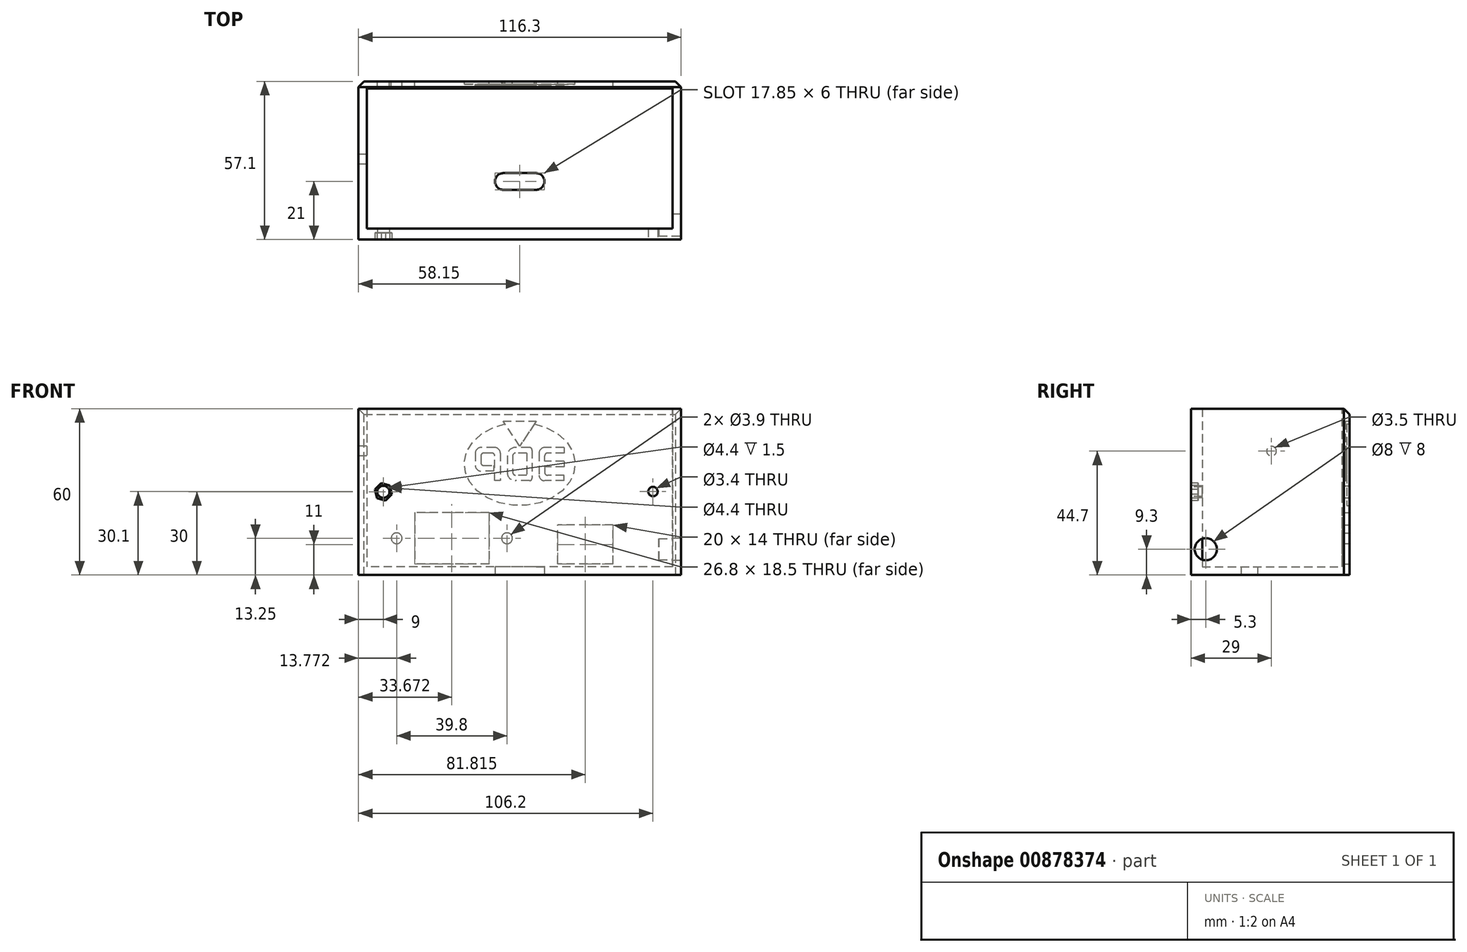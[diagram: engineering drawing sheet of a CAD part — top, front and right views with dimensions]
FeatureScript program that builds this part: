
annotation { "Feature Type Name" : "Feature", "Feature Type Description" : "" }
export const myFeature = defineFeature(function(context is Context, id is Id, definition is map)
    precondition{}
    {
        {
            var Q0;
            Q0=qCreatedBy(makeId("Front.planeOp"),FACE);
            var sketch = newSketch(context, id + "F0", { "sketchPlane" : qUnion([Q0])});
            skLineSegment(sketch, "E0.bottom", {"start": v(0, 0) * mm, "end": v(116.3, 0) * mm});
            skLineSegment(sketch, "E0.top", {"start": v(0, 70) * mm, "end": v(116.3, 70) * mm});
            skLineSegment(sketch, "E0.left", {"start": v(0, 0) * mm, "end": v(0, 70) * mm});
            skLineSegment(sketch, "E0.right", {"start": v(116.3, 0) * mm, "end": v(116.3, 70) * mm});
            skCircle(sketch, "E1", {"center": v(18, 61.5) * mm, "radius": 1.7 * mm});
            skCircle(sketch, "E2", {"center": v(103.3, 61.5) * mm, "radius": 1.7 * mm});
            skCircle(sketch, "E3", {"center": v(106.2, 5.1) * mm, "radius": 1.7 * mm});
            skCircle(sketch, "E4", {"center": v(9, 5) * mm, "radius": 2.2 * mm});
            skLineSegment(sketch, "E5.top", {"start": v(116.3, 0) * mm, "end": v(119.3, 0) * mm});
            skPoint(sketch, "E6.orphan", {"position": v(-3, 70) * mm});
            skPoint(sketch, "E7.right.end.orphan", {"position": v(-3, 35) * mm});
            skPoint(sketch, "E8.right.end.orphan", {"position": v(119.3, 35) * mm});
            skPoint(sketch, "E5.bottom.end.orphan", {"position": v(119.3, 70) * mm});
            skPoint(sketch, "E9.top.end.orphan", {"position": v(-3, 0) * mm});
            skSolve(sketch);
        }
        {
            var Q0;
            Q0=makeQuery(id+"F0.imprint","IMPRINT",FACE,{"disambiguationData":[TD([[makeQuery(id+"F0.imprint","IMPRINT",EDGE,{"derivedFrom":sQuery(id+"F0.wireOp",EDGE,"E0.bottom")}),1.0]])]});
            extrude(context, id + "F1", {"entities" : qUnion([Q0]), "oppositeDirection" : true, "depth" : 4 * mm});
        }
        {
            var Q0;
            Q0=makeQuery(id+"F1.opExtrude","CAP_FACE",FACE,{"disambiguationData":[OSD([sQuery(id+"F0.wireOp",EDGE,"E0.bottom"),sQuery(id+"F0.wireOp",EDGE,"E0.top"),sQuery(id+"F0.wireOp",EDGE,"E0.left"),sQuery(id+"F0.wireOp",EDGE,"E0.right"),sQuery(id+"F0.wireOp",EDGE,"E1"),sQuery(id+"F0.wireOp",EDGE,"E2"),sQuery(id+"F0.wireOp",EDGE,"E3"),sQuery(id+"F0.wireOp",EDGE,"E4")])],"isStart":false});
            var sketch = newSketch(context, id + "F2", { "sketchPlane" : qUnion([Q0])});
            skPoint(sketch, "E10.oppositeSnap0", {"position": v(-116.3, 35) * mm});
            skLineSegment(sketch, "E10.top", {"start": v(-116.3, 35) * mm, "end": v(-113.3, 35) * mm});
            skLineSegment(sketch, "E10.left", {"start": v(-116.3, 0) * mm, "end": v(-116.3, 35) * mm});
            skLineSegment(sketch, "E10.right", {"start": v(-113.3, 0) * mm, "end": v(-113.3, 35) * mm});
            skPoint(sketch, "E11.oppositeSnap0", {"position": v(0, 35) * mm});
            skLineSegment(sketch, "E11.top", {"start": v(0, 35) * mm, "end": v(-3, 35) * mm});
            skLineSegment(sketch, "E11.left", {"start": v(0, 0) * mm, "end": v(0, 35) * mm});
            skLineSegment(sketch, "E11.right", {"start": v(-3, 0) * mm, "end": v(-3, 35) * mm});
            skLineSegment(sketch, "E12.top", {"start": v(-116.3, -25) * mm, "end": v(-113.3, -25) * mm});
            skLineSegment(sketch, "E12.left", {"start": v(-116.3, 0) * mm, "end": v(-116.3, -25) * mm});
            skLineSegment(sketch, "E12.right", {"start": v(-113.3, 0) * mm, "end": v(-113.3, -25) * mm});
            skLineSegment(sketch, "E13.top", {"start": v(0, -25) * mm, "end": v(-3, -25) * mm});
            skLineSegment(sketch, "E13.left", {"start": v(0, 0) * mm, "end": v(0, -25) * mm});
            skLineSegment(sketch, "E13.right", {"start": v(-3, 0) * mm, "end": v(-3, -25) * mm});
            skSolve(sketch);
        }
        {
            var Q0;
            Q0=qSketchRegion(id+"F2",true);
            extrude(context, id + "F3", {"entities" : qUnion([Q0]), "operationType" : NewBodyOperationType.ADD, "depth" : 53.1 * mm});
        }
        {
            var Q0;
            Q0=makeQuery(id+"F3.boolean.opBoolean","MERGE",FACE,{"derivedFrom":[makeQuery(id+"F1.opExtrude","SWEPT_FACE",FACE,{"disambiguationData":[OSD([sQuery(id+"F0.wireOp",EDGE,"E0.left")])]}),makeQuery(id+"F3.opExtrude","SWEPT_FACE",FACE,{"disambiguationData":[OSD([sQuery(id+"F2.wireOp",EDGE,"E11.left"),sQuery(id+"F2.wireOp",EDGE,"E13.left")])]})]});
            var sketch = newSketch(context, id + "F4", { "sketchPlane" : qUnion([Q0])});
            skLineSegment(sketch, "E14", {"start": v(-57.1, 35) * mm, "end": v(-57.1, -25) * mm});
            skLineSegment(sketch, "E15", {"start": v(-57.1, -25) * mm, "end": v(0, -25) * mm});
            skLineSegment(sketch, "E16", {"start": v(0, -25) * mm, "end": v(0, 0) * mm});
            skLineSegment(sketch, "E17", {"start": v(0, 0) * mm, "end": v(-4, 0) * mm});
            skLineSegment(sketch, "E18", {"start": v(-4, 0) * mm, "end": v(-4, -22) * mm});
            skLineSegment(sketch, "E19", {"start": v(-4, -22) * mm, "end": v(-54.5, -22) * mm});
            skLineSegment(sketch, "E20", {"start": v(-54.5, -22) * mm, "end": v(-54.5, 35) * mm});
            skLineSegment(sketch, "E21", {"start": v(-54.5, 35) * mm, "end": v(-57.1, 35) * mm});
            skSolve(sketch);
        }
        {
            var Q0;
            Q0=qSketchRegion(id+"F4",true);
            extrude(context, id + "F5", {"entities" : qUnion([Q0]), "operationType" : NewBodyOperationType.ADD, "oppositeDirection" : true, "depth" : 116.3 * mm});
        }
        {
            var Q0;
            Q0=makeQuery(id+"F5.boolean.opBoolean","MERGE",FACE,{"derivedFrom":[makeQuery(id+"F3.opExtrude","CAP_FACE",FACE,{"disambiguationData":[OSD([sQuery(id+"F2.wireOp",EDGE,"E10.top"),sQuery(id+"F2.wireOp",EDGE,"E10.left"),sQuery(id+"F2.wireOp",EDGE,"E10.right"),sQuery(id+"F2.wireOp",EDGE,"E12.top"),sQuery(id+"F2.wireOp",EDGE,"E12.left"),sQuery(id+"F2.wireOp",EDGE,"E12.right")])],"isStart":false}),makeQuery(id+"F3.opExtrude","CAP_FACE",FACE,{"disambiguationData":[OSD([sQuery(id+"F2.wireOp",EDGE,"E11.top"),sQuery(id+"F2.wireOp",EDGE,"E11.left"),sQuery(id+"F2.wireOp",EDGE,"E11.right"),sQuery(id+"F2.wireOp",EDGE,"E13.top"),sQuery(id+"F2.wireOp",EDGE,"E13.left"),sQuery(id+"F2.wireOp",EDGE,"E13.right")])],"isStart":false}),makeQuery(id+"F5.opExtrude","SWEPT_FACE",FACE,{"disambiguationData":[OSD([sQuery(id+"F4.wireOp",EDGE,"E14")])]})]});
            var sketch = newSketch(context, id + "F6", { "sketchPlane" : qUnion([Q0])});
            skLineSegment(sketch, "E22.bottom", {"start": v(-47.07, -2.5) * mm, "end": v(-20.27, -2.5) * mm});
            skLineSegment(sketch, "E22.top", {"start": v(-47.07, -21) * mm, "end": v(-20.27, -21) * mm});
            skLineSegment(sketch, "E22.left", {"start": v(-47.07, -2.5) * mm, "end": v(-47.07, -21) * mm});
            skLineSegment(sketch, "E22.right", {"start": v(-20.27, -2.5) * mm, "end": v(-20.27, -21) * mm});
            skPoint(sketch, "E23.right.end.orphan", {"position": v(-79.44, -21) * mm});
            skLineSegment(sketch, "E24", {"start": v(-20.27, -11.75) * mm, "end": v(-13.77, -11.75) * mm});
            skCircle(sketch, "E25", {"center": v(-13.77, -11.75) * mm, "radius": 1.95 * mm});
            skLineSegment(sketch, "E26", {"start": v(-33.67, -2.5) * mm, "end": v(-33.67, -21) * mm, "construction": true});
            skCircle(sketch, "E27.MirrorC", {"center": v(-53.57, -11.75) * mm, "radius": 1.95 * mm});
            skLineSegment(sketch, "E28.bottom", {"start": v(-91.81, -21) * mm, "end": v(-71.81, -21) * mm});
            skLineSegment(sketch, "E28.top", {"start": v(-91.81, -7) * mm, "end": v(-71.81, -7) * mm});
            skLineSegment(sketch, "E28.left", {"start": v(-91.81, -21) * mm, "end": v(-91.81, -7) * mm});
            skLineSegment(sketch, "E28.right", {"start": v(-71.81, -21) * mm, "end": v(-71.81, -7) * mm});
            skSolve(sketch);
        }
        {
            var Q0;
            Q0=qSketchRegion(id+"F6",true);
            extrude(context, id + "F7", {"entities" : qUnion([Q0]), "operationType" : NewBodyOperationType.REMOVE, "oppositeDirection" : true, "depth" : 25 * mm});
        }
        {
            var Q0;
            Q0=makeQuery(id+"F5.boolean.opBoolean","MERGE",FACE,{"derivedFrom":[makeQuery(id+"F3.boolean.opBoolean","MERGE",FACE,{"derivedFrom":[makeQuery(id+"F1.opExtrude","SWEPT_FACE",FACE,{"disambiguationData":[OSD([sQuery(id+"F0.wireOp",EDGE,"E0.left")])]}),makeQuery(id+"F3.opExtrude","SWEPT_FACE",FACE,{"disambiguationData":[OSD([sQuery(id+"F2.wireOp",EDGE,"E11.left"),sQuery(id+"F2.wireOp",EDGE,"E13.left")])]})]}),makeQuery(id+"F5.opExtrude","CAP_FACE",FACE,{"disambiguationData":[OSD([sQuery(id+"F4.wireOp",EDGE,"E14"),sQuery(id+"F4.wireOp",EDGE,"E15"),sQuery(id+"F4.wireOp",EDGE,"E16"),sQuery(id+"F4.wireOp",EDGE,"E17"),sQuery(id+"F4.wireOp",EDGE,"E18"),sQuery(id+"F4.wireOp",EDGE,"E19"),sQuery(id+"F4.wireOp",EDGE,"E20"),sQuery(id+"F4.wireOp",EDGE,"E21")])],"isStart":true})]});
            var sketch = newSketch(context, id + "F8", { "sketchPlane" : qUnion([Q0])});
            skLineSegment(sketch, "E29", {"start": v(0, 0) * mm, "end": v(-29, 0) * mm, "construction": true});
            skLineSegment(sketch, "E30", {"start": v(-29, 0) * mm, "end": v(-29, 19.7) * mm, "construction": true});
            skCircle(sketch, "E31", {"center": v(-29, 19.7) * mm, "radius": 1.75 * mm});
            skLineSegment(sketch, "E32", {"start": v(-4, 70) * mm, "end": v(0, 70) * mm});
            skSolve(sketch);
        }
        {
            var Q0;
            Q0=makeQuery(id+"F8.imprint","IMPRINT",FACE,{"disambiguationData":[TD([[makeQuery(id+"F8.imprint","IMPRINT",EDGE,{"derivedFrom":sQuery(id+"F8.wireOp",EDGE,"E31")}),1.0]])]});
            extrude(context, id + "F9", {"entities" : qUnion([Q0]), "operationType" : NewBodyOperationType.REMOVE, "oppositeDirection" : true, "depth" : 25 * mm});
        }
        {
            var Q0;
            Q0=makeQuery(id+"F5.boolean.opBoolean","MERGE",FACE,{"derivedFrom":[makeQuery(id+"F1.opExtrude","CAP_FACE",FACE,{"disambiguationData":[OSD([sQuery(id+"F0.wireOp",EDGE,"E0.bottom"),sQuery(id+"F0.wireOp",EDGE,"E0.top"),sQuery(id+"F0.wireOp",EDGE,"E0.left"),sQuery(id+"F0.wireOp",EDGE,"E0.right"),sQuery(id+"F0.wireOp",EDGE,"E1"),sQuery(id+"F0.wireOp",EDGE,"E2"),sQuery(id+"F0.wireOp",EDGE,"E3"),sQuery(id+"F0.wireOp",EDGE,"E4")])],"isStart":false}),makeQuery(id+"F5.opExtrude","SWEPT_FACE",FACE,{"disambiguationData":[OSD([sQuery(id+"F4.wireOp",EDGE,"E18")])]})]});
            var sketch = newSketch(context, id + "F10", { "sketchPlane" : qUnion([Q0])});
            skLineSegment(sketch, "E33.bottom", {"start": v(-116.3, 70) * mm, "end": v(0, 70) * mm});
            skLineSegment(sketch, "E33.top", {"start": v(-116.3, 35) * mm, "end": v(0, 35) * mm});
            skLineSegment(sketch, "E33.left", {"start": v(-116.3, 70) * mm, "end": v(-116.3, 35) * mm});
            skLineSegment(sketch, "E33.right", {"start": v(0, 70) * mm, "end": v(0, 35) * mm});
            skSolve(sketch);
        }
        {
            var Q0;
            Q0=qSketchRegion(id+"F10",true);
            extrude(context, id + "F11", {"entities" : qUnion([Q0]), "operationType" : NewBodyOperationType.REMOVE, "oppositeDirection" : true, "depth" : 25 * mm});
        }
        {
            var Q0;
            Q0=makeQuery(id+"F5.boolean.opBoolean","MERGE",FACE,{"derivedFrom":[makeQuery(id+"F3.opExtrude","CAP_FACE",FACE,{"disambiguationData":[OSD([sQuery(id+"F2.wireOp",EDGE,"E10.top"),sQuery(id+"F2.wireOp",EDGE,"E10.left"),sQuery(id+"F2.wireOp",EDGE,"E10.right"),sQuery(id+"F2.wireOp",EDGE,"E12.top"),sQuery(id+"F2.wireOp",EDGE,"E12.left"),sQuery(id+"F2.wireOp",EDGE,"E12.right")])],"isStart":false}),makeQuery(id+"F3.opExtrude","CAP_FACE",FACE,{"disambiguationData":[OSD([sQuery(id+"F2.wireOp",EDGE,"E11.top"),sQuery(id+"F2.wireOp",EDGE,"E11.left"),sQuery(id+"F2.wireOp",EDGE,"E11.right"),sQuery(id+"F2.wireOp",EDGE,"E13.top"),sQuery(id+"F2.wireOp",EDGE,"E13.left"),sQuery(id+"F2.wireOp",EDGE,"E13.right")])],"isStart":false}),makeQuery(id+"F5.opExtrude","SWEPT_FACE",FACE,{"disambiguationData":[OSD([sQuery(id+"F4.wireOp",EDGE,"E14")])]})]});
            var sketch = newSketch(context, id + "F12", { "sketchPlane" : qUnion([Q0])});
            skLineSegment(sketch, "E34", {"start": v(-78.15, 15) * mm, "end": v(-38.15, 15) * mm, "construction": true});
            skEllipticalArc(sketch, "E35", {});
            skPoint(sketch, "E36.orphan", {"position": v(-78.15, 30) * mm});
            skPoint(sketch, "E37.orphan", {"position": v(-38.15, 30) * mm});
            skPoint(sketch, "E38.orphan", {"position": v(-38.15, 0) * mm});
            skPoint(sketch, "E39.top.start.orphan", {"position": v(-78.15, 0) * mm});
            skLineSegment(sketch, "E40.bottom", {"start": v(-74.15, 21) * mm, "end": v(-67.15, 21) * mm});
            skLineSegment(sketch, "E40.top", {"start": v(-74.15, 9) * mm, "end": v(-67.15, 9) * mm});
            skLineSegment(sketch, "E40.right", {"start": v(-65.15, 19) * mm, "end": v(-65.15, 11) * mm});
            skLineSegment(sketch, "E41.bottom", {"start": v(-61.65, 21) * mm, "end": v(-56.65, 21) * mm});
            skLineSegment(sketch, "E41.top", {"start": v(-61.65, 9) * mm, "end": v(-56.65, 9) * mm});
            skLineSegment(sketch, "E41.left", {"start": v(-62.65, 20) * mm, "end": v(-62.65, 10) * mm});
            skLineSegment(sketch, "E41.right", {"start": v(-53.65, 18) * mm, "end": v(-53.65, 12) * mm});
            skLineSegment(sketch, "E42.bottom", {"start": v(-49.15, 21) * mm, "end": v(-44.15, 21) * mm});
            skLineSegment(sketch, "E42.left", {"start": v(-51.15, 19) * mm, "end": v(-51.15, 9) * mm});
            skLineSegment(sketch, "E42.right", {"start": v(-42.15, 19) * mm, "end": v(-42.15, 14.5) * mm});
            skPoint(sketch, "E43.visualSharp", {"position": v(-65.15, 21) * mm});
            skArc(sketch, "E43.filletArc", {"start": v(-65.15, 19) * mm, "mid": v(-65.74, 20.41) * mm, "end": v(-67.15, 21) * mm});
            skPoint(sketch, "E44.visualSharp", {"position": v(-65.15, 9) * mm});
            skArc(sketch, "E44.filletArc", {"start": v(-67.15, 9) * mm, "mid": v(-65.74, 9.59) * mm, "end": v(-65.15, 11) * mm});
            skPoint(sketch, "E45.visualSharp", {"position": v(-53.65, 21) * mm});
            skArc(sketch, "E45.filletArc", {"start": v(-53.65, 18) * mm, "mid": v(-54.53, 20.12) * mm, "end": v(-56.65, 21) * mm});
            skPoint(sketch, "E46.visualSharp", {"position": v(-53.65, 9) * mm});
            skArc(sketch, "E46.filletArc", {"start": v(-56.65, 9) * mm, "mid": v(-54.53, 9.88) * mm, "end": v(-53.65, 12) * mm});
            skPoint(sketch, "E47.visualSharp", {"position": v(-51.15, 21) * mm});
            skArc(sketch, "E47.filletArc", {"start": v(-49.15, 21) * mm, "mid": v(-50.56, 20.41) * mm, "end": v(-51.15, 19) * mm});
            skPoint(sketch, "E48.visualSharp", {"position": v(-42.15, 21) * mm});
            skArc(sketch, "E48.filletArc", {"start": v(-42.15, 19) * mm, "mid": v(-42.74, 20.41) * mm, "end": v(-44.15, 21) * mm});
            skPoint(sketch, "E49.visualSharp", {"position": v(-62.65, 21) * mm});
            skArc(sketch, "E49.filletArc", {"start": v(-61.65, 21) * mm, "mid": v(-62.36, 20.7) * mm, "end": v(-62.65, 20) * mm});
            skPoint(sketch, "E50.visualSharp", {"position": v(-62.65, 9) * mm});
            skArc(sketch, "E50.filletArc", {"start": v(-62.65, 10) * mm, "mid": v(-62.36, 9.3) * mm, "end": v(-61.65, 9) * mm});
            skLineSegment(sketch, "E51.0", {"start": v(-60.65, 19) * mm, "end": v(-56.65, 19) * mm});
            skLineSegment(sketch, "E51.1", {"start": v(-60.65, 11) * mm, "end": v(-56.65, 11) * mm});
            skArc(sketch, "E51.2", {"start": v(-56.65, 11) * mm, "mid": v(-55.94, 11.3) * mm, "end": v(-55.65, 12) * mm});
            skLineSegment(sketch, "E51.3", {"start": v(-60.65, 19) * mm, "end": v(-60.65, 11) * mm});
            skLineSegment(sketch, "E51.4", {"start": v(-55.65, 18) * mm, "end": v(-55.65, 12) * mm});
            skArc(sketch, "E51.5", {"start": v(-55.65, 18) * mm, "mid": v(-55.94, 18.7) * mm, "end": v(-56.65, 19) * mm});
            skLineSegment(sketch, "E52", {"start": v(-74.15, 21) * mm, "end": v(-74.15, 19) * mm});
            skLineSegment(sketch, "E53", {"start": v(-74.15, 9) * mm, "end": v(-74.15, 11) * mm});
            skLineSegment(sketch, "E54", {"start": v(-74.15, 19) * mm, "end": v(-68.15, 19) * mm});
            skLineSegment(sketch, "E55", {"start": v(-67.15, 16) * mm, "end": v(-67.15, 18) * mm});
            skLineSegment(sketch, "E56", {"start": v(-74.15, 16) * mm, "end": v(-67.15, 16) * mm});
            skLineSegment(sketch, "E57", {"start": v(-74.15, 14) * mm, "end": v(-67.15, 14) * mm});
            skLineSegment(sketch, "E58", {"start": v(-67.15, 14) * mm, "end": v(-67.15, 12) * mm});
            skLineSegment(sketch, "E59", {"start": v(-74.15, 11) * mm, "end": v(-68.15, 11) * mm});
            skArc(sketch, "E60.filletArc", {"start": v(-68.15, 11) * mm, "mid": v(-67.44, 11.3) * mm, "end": v(-67.15, 12) * mm});
            skArc(sketch, "E61.filletArc", {"start": v(-67.15, 18) * mm, "mid": v(-67.44, 18.7) * mm, "end": v(-68.15, 19) * mm});
            skLineSegment(sketch, "E62", {"start": v(-51.15, 9) * mm, "end": v(-49.15, 9) * mm});
            skLineSegment(sketch, "E63", {"start": v(-49.15, 9) * mm, "end": v(-49.15, 18) * mm});
            skLineSegment(sketch, "E64", {"start": v(-44.15, 18) * mm, "end": v(-44.15, 15.5) * mm});
            skLineSegment(sketch, "E65", {"start": v(-45.15, 14.5) * mm, "end": v(-47.96, 14.5) * mm});
            skLineSegment(sketch, "E66", {"start": v(-47.88, 12.5) * mm, "end": v(-44.15, 12.5) * mm});
            skPoint(sketch, "E67.orphan", {"position": v(-42.15, 9) * mm});
            skLineSegment(sketch, "E68", {"start": v(-48.15, 19) * mm, "end": v(-45.15, 19) * mm});
            skPoint(sketch, "E69.visualSharp", {"position": v(-42.15, 12.5) * mm});
            skArc(sketch, "E69.filletArc", {"start": v(-44.15, 12.5) * mm, "mid": v(-42.74, 13.08) * mm, "end": v(-42.15, 14.5) * mm});
            skArc(sketch, "E70.filletArc", {"start": v(-45.15, 14.5) * mm, "mid": v(-44.44, 14.79) * mm, "end": v(-44.15, 15.5) * mm});
            skArc(sketch, "E71.filletArc", {"start": v(-44.15, 18) * mm, "mid": v(-44.44, 18.7) * mm, "end": v(-45.15, 19) * mm});
            skArc(sketch, "E72.filletArc", {"start": v(-48.15, 19) * mm, "mid": v(-48.86, 18.7) * mm, "end": v(-49.15, 18) * mm});
            skLineSegment(sketch, "E73", {"start": v(-47.96, 14.5) * mm, "end": v(-48.76, 14.5) * mm});
            skLineSegment(sketch, "E74", {"start": v(-48.76, 14.5) * mm, "end": v(-48.76, 12.5) * mm});
            skLineSegment(sketch, "E75", {"start": v(-48.76, 12.5) * mm, "end": v(-47.88, 12.5) * mm});
            skLineSegment(sketch, "E76.trimOffspring", {"start": v(-58.15, 11) * mm, "end": v(-58.15, 0) * mm, "construction": true});
            skLineSegment(sketch, "E77.trimOffspring", {"start": v(-58.15, 21) * mm, "end": v(-58.15, 19) * mm, "construction": true});
            skPoint(sketch, "E78.start.orphan", {"position": v(-58.15, 30) * mm});
            skPoint(sketch, "E79.orphan", {"position": v(-58.15, 27) * mm});
            skLineSegment(sketch, "E80", {"start": v(-58.15, 30.5) * mm, "end": v(-64.15, 30.5) * mm});
            skLineSegment(sketch, "E81", {"start": v(-64.15, 30.5) * mm, "end": v(-58.15, 21.5) * mm});
            skLineSegment(sketch, "E82", {"start": v(-58.15, 30.5) * mm, "end": v(-52.15, 30.5) * mm});
            skLineSegment(sketch, "E83", {"start": v(-58.15, 21.5) * mm, "end": v(-52.15, 30.5) * mm});
            skLineSegment(sketch, "E84", {"start": v(-74.15, 16) * mm, "end": v(-74.15, 14) * mm});
            const initialGuessF12  = {"E35": [-0.05815, 0.015, -1, 0, 0.02, 0.015, 4.981010063502463, 4.443767897266916]};
            skSetInitialGuess(sketch, initialGuessF12);
            skSolve(sketch);
        }
        {
            var Q0;
            Q0=makeQuery(id+"F12.imprint","IMPRINT",FACE,{"disambiguationData":[TD([[makeQuery(id+"F12.imprint","IMPRINT",EDGE,{"derivedFrom":sQuery(id+"F12.wireOp",EDGE,"E40.bottom")}),-1.0]])]});
            var Q1;
            Q1=makeQuery(id+"F12.imprint","IMPRINT",FACE,{"disambiguationData":[TD([[makeQuery(id+"F12.imprint","IMPRINT",EDGE,{"derivedFrom":sQuery(id+"F12.wireOp",EDGE,"E41.bottom")}),-1.0]])]});
            var Q2;
            Q2=makeQuery(id+"F12.imprint","IMPRINT",FACE,{"disambiguationData":[TD([[makeQuery(id+"F12.imprint","IMPRINT",EDGE,{"derivedFrom":sQuery(id+"F12.wireOp",EDGE,"E42.bottom")}),-1.0]])]});
            extrude(context, id + "F13", {"entities" : qUnion([Q0, Q1, Q2]), "operationType" : NewBodyOperationType.REMOVE, "oppositeDirection" : true, "depth" : 1.5 * mm});
        }
        {
            var Q0;
            {var subQ7=sQuery(id+"F4.wireOp",EDGE,"E14");var subQ8=sQuery(id+"F2.wireOp",EDGE,"E12.top");var subQ9=sQuery(id+"F2.wireOp",EDGE,"E13.left");var subQ10=sQuery(id+"F2.wireOp",EDGE,"E11.left");var subQ11=sQuery(id+"F2.wireOp",EDGE,"E11.top");var subQ12=sQuery(id+"F2.wireOp",EDGE,"E13.top");var subQ13=sQuery(id+"F2.wireOp",EDGE,"E10.top");var subQ14=sQuery(id+"F2.wireOp",EDGE,"E12.left");var subQ15=sQuery(id+"F2.wireOp",EDGE,"E10.left");Q0=makeQuery(id+"F13.boolean.opBoolean","SPLIT",FACE,{"disambiguationData":[TD([makeQuery(id+"F1.opExtrude","SWEPT_FACE",FACE,{"disambiguationData":[OSD([sQuery(id+"F0.wireOp",EDGE,"E0.left")])]})])],"derivedFrom":makeQuery(id+"F5.boolean.opBoolean","MERGE",FACE,{"derivedFrom":[makeQuery(id+"F3.opExtrude","CAP_FACE",FACE,{"disambiguationData":[OSD([subQ13,subQ15,sQuery(id+"F2.wireOp",EDGE,"E10.right"),subQ8,subQ14,sQuery(id+"F2.wireOp",EDGE,"E12.right")])],"isStart":false}),makeQuery(id+"F3.opExtrude","CAP_FACE",FACE,{"disambiguationData":[OSD([subQ11,subQ10,sQuery(id+"F2.wireOp",EDGE,"E11.right"),subQ12,subQ9,sQuery(id+"F2.wireOp",EDGE,"E13.right")])],"isStart":false}),makeQuery(id+"F5.opExtrude","SWEPT_FACE",FACE,{"disambiguationData":[OSD([subQ7])]})]})});}
            var sketch = newSketch(context, id + "F14", { "sketchPlane" : qUnion([Q0])});
            skEllipticalArc(sketch, "E85.1", {});
            skPoint(sketch, "E85.2", {"position": v(-78.15, 30) * mm});
            skPoint(sketch, "E85.3", {"position": v(-38.15, 30) * mm});
            skPoint(sketch, "E85.4", {"position": v(-38.15, 0) * mm});
            skPoint(sketch, "E85.5", {"position": v(-78.15, 0) * mm});
            skLineSegment(sketch, "E85.6", {"start": v(-74.15, 21) * mm, "end": v(-67.15, 21) * mm});
            skLineSegment(sketch, "E85.7", {"start": v(-74.15, 9) * mm, "end": v(-67.15, 9) * mm});
            skLineSegment(sketch, "E85.8", {"start": v(-65.15, 19) * mm, "end": v(-65.15, 11) * mm});
            skLineSegment(sketch, "E85.9", {"start": v(-61.65, 21) * mm, "end": v(-56.65, 21) * mm});
            skLineSegment(sketch, "E85.10", {"start": v(-61.65, 9) * mm, "end": v(-56.65, 9) * mm});
            skLineSegment(sketch, "E85.11", {"start": v(-62.65, 20) * mm, "end": v(-62.65, 10) * mm});
            skLineSegment(sketch, "E85.12", {"start": v(-53.65, 18) * mm, "end": v(-53.65, 12) * mm});
            skLineSegment(sketch, "E85.13", {"start": v(-49.15, 21) * mm, "end": v(-44.15, 21) * mm});
            skLineSegment(sketch, "E85.14", {"start": v(-51.15, 19) * mm, "end": v(-51.15, 9) * mm});
            skLineSegment(sketch, "E85.15", {"start": v(-42.15, 19) * mm, "end": v(-42.15, 14.5) * mm});
            skPoint(sketch, "E85.16", {"position": v(-65.15, 21) * mm});
            skArc(sketch, "E85.17", {"start": v(-65.15, 19) * mm, "mid": v(-65.74, 20.41) * mm, "end": v(-67.15, 21) * mm});
            skPoint(sketch, "E85.18", {"position": v(-65.15, 9) * mm});
            skArc(sketch, "E85.19", {"start": v(-67.15, 9) * mm, "mid": v(-65.74, 9.59) * mm, "end": v(-65.15, 11) * mm});
            skPoint(sketch, "E85.20", {"position": v(-53.65, 21) * mm});
            skArc(sketch, "E85.21", {"start": v(-53.65, 18) * mm, "mid": v(-54.53, 20.12) * mm, "end": v(-56.65, 21) * mm});
            skPoint(sketch, "E85.22", {"position": v(-53.65, 9) * mm});
            skArc(sketch, "E85.23", {"start": v(-56.65, 9) * mm, "mid": v(-54.53, 9.88) * mm, "end": v(-53.65, 12) * mm});
            skPoint(sketch, "E85.24", {"position": v(-51.15, 21) * mm});
            skArc(sketch, "E85.25", {"start": v(-49.15, 21) * mm, "mid": v(-50.56, 20.41) * mm, "end": v(-51.15, 19) * mm});
            skPoint(sketch, "E85.26", {"position": v(-42.15, 21) * mm});
            skArc(sketch, "E85.27", {"start": v(-42.15, 19) * mm, "mid": v(-42.74, 20.41) * mm, "end": v(-44.15, 21) * mm});
            skPoint(sketch, "E85.28", {"position": v(-62.65, 21) * mm});
            skArc(sketch, "E85.29", {"start": v(-61.65, 21) * mm, "mid": v(-62.36, 20.7) * mm, "end": v(-62.65, 20) * mm});
            skPoint(sketch, "E85.30", {"position": v(-62.65, 9) * mm});
            skArc(sketch, "E85.31", {"start": v(-62.65, 10) * mm, "mid": v(-62.36, 9.3) * mm, "end": v(-61.65, 9) * mm});
            skLineSegment(sketch, "E85.33", {"start": v(-60.65, 11) * mm, "end": v(-56.65, 11) * mm});
            skArc(sketch, "E85.34", {"start": v(-56.65, 11) * mm, "mid": v(-55.94, 11.3) * mm, "end": v(-55.65, 12) * mm});
            skLineSegment(sketch, "E85.35", {"start": v(-60.65, 15) * mm, "end": v(-60.65, 11) * mm});
            skLineSegment(sketch, "E85.36", {"start": v(-55.65, 18) * mm, "end": v(-55.65, 12) * mm});
            skArc(sketch, "E85.37", {"start": v(-55.65, 18) * mm, "mid": v(-55.94, 18.7) * mm, "end": v(-56.65, 19) * mm});
            skLineSegment(sketch, "E85.38", {"start": v(-74.15, 21) * mm, "end": v(-74.15, 19) * mm});
            skLineSegment(sketch, "E85.39", {"start": v(-74.15, 9) * mm, "end": v(-74.15, 11) * mm});
            skLineSegment(sketch, "E85.40", {"start": v(-74.15, 19) * mm, "end": v(-68.15, 19) * mm});
            skLineSegment(sketch, "E85.41", {"start": v(-67.15, 16) * mm, "end": v(-67.15, 18) * mm});
            skLineSegment(sketch, "E85.42", {"start": v(-74.15, 16) * mm, "end": v(-67.15, 16) * mm});
            skLineSegment(sketch, "E85.43", {"start": v(-74.15, 14) * mm, "end": v(-67.15, 14) * mm});
            skLineSegment(sketch, "E85.44", {"start": v(-67.15, 14) * mm, "end": v(-67.15, 12) * mm});
            skLineSegment(sketch, "E85.45", {"start": v(-74.15, 11) * mm, "end": v(-68.15, 11) * mm});
            skPoint(sketch, "E85.46", {"position": v(-67.15, 11) * mm});
            skArc(sketch, "E85.47", {"start": v(-68.15, 11) * mm, "mid": v(-67.44, 11.3) * mm, "end": v(-67.15, 12) * mm});
            skPoint(sketch, "E85.48", {"position": v(-67.15, 19) * mm});
            skArc(sketch, "E85.49", {"start": v(-67.15, 18) * mm, "mid": v(-67.44, 18.7) * mm, "end": v(-68.15, 19) * mm});
            skLineSegment(sketch, "E85.50", {"start": v(-51.15, 9) * mm, "end": v(-49.15, 9) * mm});
            skLineSegment(sketch, "E85.51", {"start": v(-49.15, 9) * mm, "end": v(-49.15, 18) * mm});
            skLineSegment(sketch, "E85.52", {"start": v(-44.15, 18) * mm, "end": v(-44.15, 15.5) * mm});
            skLineSegment(sketch, "E85.53", {"start": v(-45.15, 14.5) * mm, "end": v(-47.96, 14.5) * mm});
            skLineSegment(sketch, "E85.54", {"start": v(-47.88, 12.5) * mm, "end": v(-44.15, 12.5) * mm});
            skPoint(sketch, "E85.55", {"position": v(-42.15, 9) * mm});
            skLineSegment(sketch, "E85.56", {"start": v(-48.15, 19) * mm, "end": v(-45.15, 19) * mm});
            skPoint(sketch, "E85.57", {"position": v(-42.15, 12.5) * mm});
            skArc(sketch, "E85.58", {"start": v(-44.15, 12.5) * mm, "mid": v(-42.74, 13.08) * mm, "end": v(-42.15, 14.5) * mm});
            skPoint(sketch, "E85.59", {"position": v(-44.15, 14.5) * mm});
            skArc(sketch, "E85.60", {"start": v(-45.15, 14.5) * mm, "mid": v(-44.44, 14.79) * mm, "end": v(-44.15, 15.5) * mm});
            skPoint(sketch, "E85.61", {"position": v(-44.15, 19) * mm});
            skArc(sketch, "E85.62", {"start": v(-44.15, 18) * mm, "mid": v(-44.44, 18.7) * mm, "end": v(-45.15, 19) * mm});
            skPoint(sketch, "E85.63", {"position": v(-49.15, 19) * mm});
            skArc(sketch, "E85.64", {"start": v(-48.15, 19) * mm, "mid": v(-48.86, 18.7) * mm, "end": v(-49.15, 18) * mm});
            skLineSegment(sketch, "E85.65", {"start": v(-47.96, 14.5) * mm, "end": v(-48.76, 14.5) * mm});
            skLineSegment(sketch, "E85.66", {"start": v(-48.76, 14.5) * mm, "end": v(-48.76, 12.5) * mm});
            skLineSegment(sketch, "E85.67", {"start": v(-48.76, 12.5) * mm, "end": v(-47.88, 12.5) * mm});
            skPoint(sketch, "E85.70", {"position": v(-58.15, 30) * mm});
            skPoint(sketch, "E85.71", {"position": v(-58.15, 27) * mm});
            skLineSegment(sketch, "E85.72", {"start": v(-58.15, 30.5) * mm, "end": v(-64.15, 30.5) * mm});
            skLineSegment(sketch, "E85.73", {"start": v(-64.15, 30.5) * mm, "end": v(-58.15, 21.5) * mm});
            skLineSegment(sketch, "E85.74", {"start": v(-58.15, 30.5) * mm, "end": v(-52.15, 30.5) * mm});
            skLineSegment(sketch, "E85.75", {"start": v(-58.15, 21.5) * mm, "end": v(-52.15, 30.5) * mm});
            skLineSegment(sketch, "E85.76", {"start": v(-74.15, 16) * mm, "end": v(-74.15, 14) * mm});
            skPoint(sketch, "E85.69.end.orphan", {"position": v(-58.15, 19) * mm});
            skPoint(sketch, "E85.69.start.orphan", {"position": v(-58.15, 21) * mm});
            skPoint(sketch, "E86.orphan", {"position": v(-60.65, 19) * mm});
            skPoint(sketch, "E85.32.end.orphan", {"position": v(-56.65, 19) * mm});
            skPoint(sketch, "E87.orphan", {"position": v(-58.15, 0) * mm});
            skPoint(sketch, "E85.68.start.orphan", {"position": v(-58.15, 11) * mm});
            skPoint(sketch, "E88.trimOffspring.end.orphan", {"position": v(-38.15, 15) * mm});
            skPoint(sketch, "E85.0.start.orphan", {"position": v(-78.15, 15) * mm});
            const initialGuessF14  = {"E85.1": [-0.05815, 0.015, -1, 0, 0.02, 0.015, 4.981010063502463, 4.443767897266916]};
            skSetInitialGuess(sketch, initialGuessF14);
            skSolve(sketch);
        }
        {
            var Q0;
            {var subQ0=sQuery(id+"F14.wireOp",EDGE,"E85.1");Q0=makeQuery(id+"F14.imprint","IMPRINT",FACE,{"disambiguationData":[TD([[makeQuery(id+"F14.imprint","IMPRINT",EDGE,{"derivedFrom":subQ0}),1.0]])]});}
            extrude(context, id + "F15", {"entities" : qUnion([Q0]), "operationType" : NewBodyOperationType.REMOVE, "oppositeDirection" : true, "depth" : 1 * mm});
        }
        {
            var Q0;
            Q0=makeQuery(id+"F13.boolean.opBoolean","SPLIT",FACE,{"disambiguationData":[TD([makeQuery(id+"F13.opExtrude","SWEPT_FACE",FACE,{"disambiguationData":[OSD([sQuery(id+"F12.wireOp",EDGE,"E51.0")])]})])],"derivedFrom":makeQuery(id+"F5.boolean.opBoolean","MERGE",FACE,{"derivedFrom":[makeQuery(id+"F3.opExtrude","CAP_FACE",FACE,{"disambiguationData":[OSD([sQuery(id+"F2.wireOp",EDGE,"E10.top"),sQuery(id+"F2.wireOp",EDGE,"E10.left"),sQuery(id+"F2.wireOp",EDGE,"E10.right"),sQuery(id+"F2.wireOp",EDGE,"E12.top"),sQuery(id+"F2.wireOp",EDGE,"E12.left"),sQuery(id+"F2.wireOp",EDGE,"E12.right")])],"isStart":false}),makeQuery(id+"F3.opExtrude","CAP_FACE",FACE,{"disambiguationData":[OSD([sQuery(id+"F2.wireOp",EDGE,"E11.top"),sQuery(id+"F2.wireOp",EDGE,"E11.left"),sQuery(id+"F2.wireOp",EDGE,"E11.right"),sQuery(id+"F2.wireOp",EDGE,"E13.top"),sQuery(id+"F2.wireOp",EDGE,"E13.left"),sQuery(id+"F2.wireOp",EDGE,"E13.right")])],"isStart":false}),makeQuery(id+"F5.opExtrude","SWEPT_FACE",FACE,{"disambiguationData":[OSD([sQuery(id+"F4.wireOp",EDGE,"E14")])]})]})});
            extrude(context, id + "F16", {"entities" : qUnion([Q0]), "operationType" : NewBodyOperationType.REMOVE, "oppositeDirection" : true, "depth" : 1 * mm});
        }
        {
            var Q0;
            {var subQ7=sQuery(id+"F4.wireOp",EDGE,"E14");var subQ8=sQuery(id+"F2.wireOp",EDGE,"E12.top");var subQ9=sQuery(id+"F2.wireOp",EDGE,"E13.left");var subQ10=sQuery(id+"F2.wireOp",EDGE,"E11.left");var subQ11=sQuery(id+"F2.wireOp",EDGE,"E11.top");var subQ12=sQuery(id+"F2.wireOp",EDGE,"E13.top");var subQ13=sQuery(id+"F2.wireOp",EDGE,"E10.top");var subQ14=sQuery(id+"F2.wireOp",EDGE,"E12.left");var subQ15=sQuery(id+"F2.wireOp",EDGE,"E10.left");Q0=makeQuery(id+"F13.boolean.opBoolean","SPLIT",FACE,{"disambiguationData":[TD([makeQuery(id+"F1.opExtrude","SWEPT_FACE",FACE,{"disambiguationData":[OSD([sQuery(id+"F0.wireOp",EDGE,"E0.left")])]})])],"derivedFrom":makeQuery(id+"F5.boolean.opBoolean","MERGE",FACE,{"derivedFrom":[makeQuery(id+"F3.opExtrude","CAP_FACE",FACE,{"disambiguationData":[OSD([subQ13,subQ15,sQuery(id+"F2.wireOp",EDGE,"E10.right"),subQ8,subQ14,sQuery(id+"F2.wireOp",EDGE,"E12.right")])],"isStart":false}),makeQuery(id+"F3.opExtrude","CAP_FACE",FACE,{"disambiguationData":[OSD([subQ11,subQ10,sQuery(id+"F2.wireOp",EDGE,"E11.right"),subQ12,subQ9,sQuery(id+"F2.wireOp",EDGE,"E13.right")])],"isStart":false}),makeQuery(id+"F5.opExtrude","SWEPT_FACE",FACE,{"disambiguationData":[OSD([subQ7])]})]})});}
            var sketch = newSketch(context, id + "F17", { "sketchPlane" : qUnion([Q0])});
            skPoint(sketch, "E89.2", {"position": v(-78.15, 30) * mm});
            skPoint(sketch, "E89.3", {"position": v(-38.15, 30) * mm});
            skPoint(sketch, "E89.4", {"position": v(-38.15, 0) * mm});
            skPoint(sketch, "E89.5", {"position": v(-78.15, 0) * mm});
            skPoint(sketch, "E89.16", {"position": v(-65.15, 21) * mm});
            skPoint(sketch, "E89.18", {"position": v(-65.15, 9) * mm});
            skPoint(sketch, "E89.20", {"position": v(-53.65, 21) * mm});
            skPoint(sketch, "E89.22", {"position": v(-53.65, 9) * mm});
            skPoint(sketch, "E89.24", {"position": v(-51.15, 21) * mm});
            skPoint(sketch, "E89.26", {"position": v(-42.15, 21) * mm});
            skPoint(sketch, "E89.28", {"position": v(-62.65, 21) * mm});
            skPoint(sketch, "E89.30", {"position": v(-62.65, 9) * mm});
            skPoint(sketch, "E89.46", {"position": v(-67.15, 11) * mm});
            skPoint(sketch, "E89.48", {"position": v(-67.15, 19) * mm});
            skPoint(sketch, "E89.55", {"position": v(-42.15, 9) * mm});
            skPoint(sketch, "E89.57", {"position": v(-42.15, 12.5) * mm});
            skPoint(sketch, "E89.59", {"position": v(-44.15, 14.5) * mm});
            skPoint(sketch, "E89.61", {"position": v(-44.15, 19) * mm});
            skPoint(sketch, "E89.63", {"position": v(-49.15, 19) * mm});
            skPoint(sketch, "E89.70", {"position": v(-58.15, 30) * mm});
            skPoint(sketch, "E89.71", {"position": v(-58.15, 27) * mm});
            skLineSegment(sketch, "E89.72", {"start": v(-58.15, 30.5) * mm, "end": v(-64.15, 30.5) * mm});
            skLineSegment(sketch, "E89.73", {"start": v(-64.15, 30.5) * mm, "end": v(-58.15, 21.5) * mm});
            skLineSegment(sketch, "E89.74", {"start": v(-58.15, 30.5) * mm, "end": v(-52.15, 30.5) * mm});
            skLineSegment(sketch, "E89.75", {"start": v(-58.15, 21.5) * mm, "end": v(-52.15, 30.5) * mm});
            skPoint(sketch, "E90.orphan", {"position": v(-63.46, 29.46) * mm});
            skPoint(sketch, "E91.orphan", {"position": v(-78.15, 15) * mm});
            skPoint(sketch, "E89.45.end.orphan", {"position": v(-68.15, 11) * mm});
            skPoint(sketch, "E89.45.start.orphan", {"position": v(-74.15, 11) * mm});
            skPoint(sketch, "E89.6.end.orphan", {"position": v(-67.15, 21) * mm});
            skPoint(sketch, "E89.6.start.orphan", {"position": v(-74.15, 21) * mm});
            skPoint(sketch, "E89.68.start.orphan", {"position": v(-58.15, 11) * mm});
            skPoint(sketch, "E89.34.end.orphan", {"position": v(-55.65, 12) * mm});
            skPoint(sketch, "E89.34.start.orphan", {"position": v(-56.65, 11) * mm});
            skPoint(sketch, "E89.36.start.orphan", {"position": v(-55.65, 18) * mm});
            skPoint(sketch, "E89.37.end.orphan", {"position": v(-56.65, 19) * mm});
            skPoint(sketch, "E89.37.start.orphan", {"position": v(-55.65, 18) * mm});
            skPoint(sketch, "E89.32.start.orphan", {"position": v(-60.65, 19) * mm});
            skPoint(sketch, "E89.69.end.orphan", {"position": v(-58.15, 19) * mm});
            skPoint(sketch, "E89.69.start.orphan", {"position": v(-58.15, 21) * mm});
            skPoint(sketch, "E89.40.end.orphan", {"position": v(-68.15, 19) * mm});
            skPoint(sketch, "E89.40.start.orphan", {"position": v(-74.15, 19) * mm});
            skPoint(sketch, "E89.38.end.orphan", {"position": v(-74.15, 19) * mm});
            skPoint(sketch, "E89.38.start.orphan", {"position": v(-74.15, 21) * mm});
            skPoint(sketch, "E89.49.end.orphan", {"position": v(-68.15, 19) * mm});
            skPoint(sketch, "E89.49.start.orphan", {"position": v(-67.15, 18) * mm});
            skPoint(sketch, "E89.17.end.orphan", {"position": v(-67.15, 21) * mm});
            skPoint(sketch, "E89.17.start.orphan", {"position": v(-65.15, 19) * mm});
            skPoint(sketch, "E89.41.end.orphan", {"position": v(-67.15, 18) * mm});
            skPoint(sketch, "E89.41.start.orphan", {"position": v(-67.15, 16) * mm});
            skPoint(sketch, "E89.42.end.orphan", {"position": v(-67.15, 16) * mm});
            skPoint(sketch, "E89.42.start.orphan", {"position": v(-74.15, 16) * mm});
            skPoint(sketch, "E89.43.end.orphan", {"position": v(-67.15, 14) * mm});
            skPoint(sketch, "E89.43.start.orphan", {"position": v(-74.15, 14) * mm});
            skPoint(sketch, "E89.76.end.orphan", {"position": v(-74.15, 14) * mm});
            skPoint(sketch, "E89.44.end.orphan", {"position": v(-67.15, 12) * mm});
            skPoint(sketch, "E89.44.start.orphan", {"position": v(-67.15, 14) * mm});
            skPoint(sketch, "E89.47.end.orphan", {"position": v(-67.15, 12) * mm});
            skPoint(sketch, "E89.47.start.orphan", {"position": v(-68.15, 11) * mm});
            skPoint(sketch, "E89.39.end.orphan", {"position": v(-74.15, 11) * mm});
            skPoint(sketch, "E89.39.start.orphan", {"position": v(-74.15, 9) * mm});
            skPoint(sketch, "E89.7.end.orphan", {"position": v(-67.15, 9) * mm});
            skPoint(sketch, "E89.7.start.orphan", {"position": v(-74.15, 9) * mm});
            skPoint(sketch, "E89.19.end.orphan", {"position": v(-65.15, 11) * mm});
            skPoint(sketch, "E89.19.start.orphan", {"position": v(-67.15, 9) * mm});
            skPoint(sketch, "E89.8.end.orphan", {"position": v(-65.15, 11) * mm});
            skPoint(sketch, "E89.11.end.orphan", {"position": v(-62.65, 10) * mm});
            skPoint(sketch, "E89.35.end.orphan", {"position": v(-60.65, 11) * mm});
            skPoint(sketch, "E89.33.end.orphan", {"position": v(-56.65, 11) * mm});
            skPoint(sketch, "E89.10.end.orphan", {"position": v(-56.65, 9) * mm});
            skPoint(sketch, "E89.10.start.orphan", {"position": v(-61.65, 9) * mm});
            skPoint(sketch, "E89.23.end.orphan", {"position": v(-53.65, 12) * mm});
            skPoint(sketch, "E89.23.start.orphan", {"position": v(-56.65, 9) * mm});
            skPoint(sketch, "E89.12.start.orphan", {"position": v(-53.65, 18) * mm});
            skPoint(sketch, "E89.21.end.orphan", {"position": v(-56.65, 21) * mm});
            skPoint(sketch, "E89.21.start.orphan", {"position": v(-53.65, 18) * mm});
            skPoint(sketch, "E89.9.end.orphan", {"position": v(-56.65, 21) * mm});
            skPoint(sketch, "E89.29.end.orphan", {"position": v(-62.65, 20) * mm});
            skPoint(sketch, "E89.29.start.orphan", {"position": v(-61.65, 21) * mm});
            skPoint(sketch, "E89.31.end.orphan", {"position": v(-61.65, 9) * mm});
            skPoint(sketch, "E89.31.start.orphan", {"position": v(-62.65, 10) * mm});
            skPoint(sketch, "E89.50.end.orphan", {"position": v(-49.15, 9) * mm});
            skPoint(sketch, "E89.50.start.orphan", {"position": v(-51.15, 9) * mm});
            skPoint(sketch, "E89.14.start.orphan", {"position": v(-51.15, 19) * mm});
            skPoint(sketch, "E89.25.end.orphan", {"position": v(-51.15, 19) * mm});
            skPoint(sketch, "E89.25.start.orphan", {"position": v(-49.15, 21) * mm});
            skPoint(sketch, "E89.13.end.orphan", {"position": v(-44.15, 21) * mm});
            skPoint(sketch, "E89.13.start.orphan", {"position": v(-49.15, 21) * mm});
            skPoint(sketch, "E89.27.end.orphan", {"position": v(-44.15, 21) * mm});
            skPoint(sketch, "E89.27.start.orphan", {"position": v(-42.15, 19) * mm});
            skPoint(sketch, "E92.orphan", {"position": v(-58.15, 0) * mm});
            skPoint(sketch, "E89.1.end.orphan", {"position": v(-52.84, 29.46) * mm});
            skPoint(sketch, "E89.56.end.orphan", {"position": v(-45.15, 19) * mm});
            skPoint(sketch, "E89.56.start.orphan", {"position": v(-48.15, 19) * mm});
            skPoint(sketch, "E89.64.end.orphan", {"position": v(-49.15, 18) * mm});
            skPoint(sketch, "E89.64.start.orphan", {"position": v(-48.15, 19) * mm});
            skPoint(sketch, "E89.62.end.orphan", {"position": v(-45.15, 19) * mm});
            skPoint(sketch, "E89.62.start.orphan", {"position": v(-44.15, 18) * mm});
            skPoint(sketch, "E89.52.end.orphan", {"position": v(-44.15, 15.5) * mm});
            skPoint(sketch, "E89.52.start.orphan", {"position": v(-44.15, 18) * mm});
            skPoint(sketch, "E93.trimOffspring.end.orphan", {"position": v(-38.15, 15) * mm});
            skPoint(sketch, "E89.60.end.orphan", {"position": v(-44.15, 15.5) * mm});
            skPoint(sketch, "E89.53.end.orphan", {"position": v(-47.96, 14.5) * mm});
            skPoint(sketch, "E89.53.start.orphan", {"position": v(-45.15, 14.5) * mm});
            skPoint(sketch, "E89.51.start.orphan", {"position": v(-49.15, 9) * mm});
            skPoint(sketch, "E89.66.end.orphan", {"position": v(-48.76, 12.5) * mm});
            skPoint(sketch, "E89.66.start.orphan", {"position": v(-48.76, 14.5) * mm});
            skPoint(sketch, "E89.65.end.orphan", {"position": v(-48.76, 14.5) * mm});
            skPoint(sketch, "E89.65.start.orphan", {"position": v(-47.96, 14.5) * mm});
            skPoint(sketch, "E89.67.end.orphan", {"position": v(-47.88, 12.5) * mm});
            skPoint(sketch, "E89.67.start.orphan", {"position": v(-48.76, 12.5) * mm});
            skPoint(sketch, "E89.54.end.orphan", {"position": v(-44.15, 12.5) * mm});
            skPoint(sketch, "E89.54.start.orphan", {"position": v(-47.88, 12.5) * mm});
            skPoint(sketch, "E89.58.end.orphan", {"position": v(-42.15, 14.5) * mm});
            skPoint(sketch, "E89.58.start.orphan", {"position": v(-44.15, 12.5) * mm});
            skPoint(sketch, "E89.15.end.orphan", {"position": v(-42.15, 14.5) * mm});
            skSolve(sketch);
        }
        {
            var Q0;
            {var subQ6=sQuery(id+"F17.wireOp",EDGE,"E89.72");Q0=makeQuery(id+"F17.imprint","IMPRINT",FACE,{"disambiguationData":[TD([[makeQuery(id+"F17.imprint","IMPRINT",EDGE,{"derivedFrom":subQ6}),1.0]])]});}
            extrude(context, id + "F18", {"entities" : qUnion([Q0]), "operationType" : NewBodyOperationType.REMOVE, "oppositeDirection" : true, "depth" : 1.5 * mm});
        }
        {
            var Q0;
            Q0=makeQuery(id+"F5.boolean.opBoolean","MERGE",FACE,{"derivedFrom":[makeQuery(id+"F3.opExtrude","SWEPT_FACE",FACE,{"disambiguationData":[OSD([sQuery(id+"F2.wireOp",EDGE,"E12.top")])]}),makeQuery(id+"F3.opExtrude","SWEPT_FACE",FACE,{"disambiguationData":[OSD([sQuery(id+"F2.wireOp",EDGE,"E13.top")])]}),makeQuery(id+"F5.opExtrude","SWEPT_FACE",FACE,{"disambiguationData":[OSD([sQuery(id+"F4.wireOp",EDGE,"E15")])]})]});
            var sketch = newSketch(context, id + "F19", { "sketchPlane" : qUnion([Q0])});
            skLineSegment(sketch, "E94.0", {"start": v(52.22, -24) * mm, "end": v(64.07, -24) * mm});
            skLineSegment(sketch, "E95.MirrorCS", {"start": v(52.23, -18) * mm, "end": v(64.07, -18) * mm});
            skArc(sketch, "E96", {"start": v(52.23, -18) * mm, "mid": v(49.23, -21) * mm, "end": v(52.22, -24) * mm});
            skArc(sketch, "E97", {"start": v(64.07, -24) * mm, "mid": v(67.07, -21) * mm, "end": v(64.07, -18) * mm});
            skPoint(sketch, "E98.orphan", {"position": v(58.15, 0) * mm});
            skSolve(sketch);
        }
        {
            var Q0;
            Q0=qSketchRegion(id+"F19",true);
            extrude(context, id + "F20", {"entities" : qUnion([Q0]), "operationType" : NewBodyOperationType.REMOVE, "oppositeDirection" : true, "depth" : 25 * mm});
        }
        {
            var Q0;
            Q0=makeQuery(id+"F3.opExtrude","CAP_EDGE",EDGE,{"disambiguationData":[OSD([sQuery(id+"F2.wireOp",EDGE,"E10.left"),sQuery(id+"F2.wireOp",EDGE,"E12.left")])],"isStart":false});
            var Q1;
            Q1=makeQuery(id+"F3.opExtrude","CAP_EDGE",EDGE,{"disambiguationData":[OSD([sQuery(id+"F2.wireOp",EDGE,"E11.left"),sQuery(id+"F2.wireOp",EDGE,"E13.left")])],"isStart":false});
            var Q2;
            Q2=makeQuery(id+"F5.boolean.opBoolean","MERGE",EDGE,{"derivedFrom":[makeQuery(id+"F3.opExtrude","CAP_EDGE",EDGE,{"disambiguationData":[OSD([sQuery(id+"F2.wireOp",EDGE,"E10.top")])],"isStart":false}),makeQuery(id+"F3.opExtrude","CAP_EDGE",EDGE,{"disambiguationData":[OSD([sQuery(id+"F2.wireOp",EDGE,"E11.top")])],"isStart":false}),makeQuery(id+"F5.opExtrude","SWEPT_EDGE",EDGE,{"disambiguationData":[OSD([sQuery(id+"F4.wireOp",EDGE,"E14"),sQuery(id+"F4.wireOp",EDGE,"E21")])]})]});
            chamfer(context, id + "F21", {"entities" : qUnion([Q0, Q1, Q2]), "width" : 2 * mm, "tangentPropagation" : true});
        }
        {
            var Q0;
            Q0=makeQuery(id+"F5.boolean.opBoolean","MERGE",FACE,{"derivedFrom":[makeQuery(id+"F1.opExtrude","CAP_FACE",FACE,{"disambiguationData":[OSD([sQuery(id+"F0.wireOp",EDGE,"E0.bottom"),sQuery(id+"F0.wireOp",EDGE,"E0.top"),sQuery(id+"F0.wireOp",EDGE,"E0.left"),sQuery(id+"F0.wireOp",EDGE,"E0.right"),sQuery(id+"F0.wireOp",EDGE,"E1"),sQuery(id+"F0.wireOp",EDGE,"E2"),sQuery(id+"F0.wireOp",EDGE,"E3"),sQuery(id+"F0.wireOp",EDGE,"E4")])],"isStart":true}),makeQuery(id+"F5.opExtrude","SWEPT_FACE",FACE,{"disambiguationData":[OSD([sQuery(id+"F4.wireOp",EDGE,"E16")])]})]});
            var sketch = newSketch(context, id + "F22", { "sketchPlane" : qUnion([Q0])});
            skCircle(sketch, "E99.0", {"center": v(9, 5) * mm, "radius": 2.8 * mm});
            skLineSegment(sketch, "E99.1", {"start": v(11.33, 7.24) * mm, "end": v(8.23, 8.14) * mm});
            skLineSegment(sketch, "E99.2", {"start": v(8.23, 8.14) * mm, "end": v(5.9, 5.9) * mm});
            skLineSegment(sketch, "E99.3", {"start": v(5.9, 5.9) * mm, "end": v(6.67, 2.76) * mm});
            skLineSegment(sketch, "E99.4", {"start": v(6.67, 2.76) * mm, "end": v(9.77, 1.86) * mm});
            skLineSegment(sketch, "E99.5", {"start": v(9.77, 1.86) * mm, "end": v(12.1, 4.1) * mm});
            skLineSegment(sketch, "E99.6", {"start": v(12.1, 4.1) * mm, "end": v(11.33, 7.24) * mm});
            skPoint(sketch, "E99.7", {"position": v(9.78, 7.69) * mm});
            skSolve(sketch);
        }
        {
            var Q0;
            Q0=qSketchRegion(id+"F22",true);
            extrude(context, id + "F23", {"entities" : qUnion([Q0]), "operationType" : NewBodyOperationType.REMOVE, "oppositeDirection" : true, "depth" : 2.5 * mm});
        }
        {
            var Q0;
            {var subQ7=sQuery(id+"F4.wireOp",EDGE,"E14");var subQ8=sQuery(id+"F2.wireOp",EDGE,"E12.top");var subQ9=sQuery(id+"F2.wireOp",EDGE,"E13.left");var subQ10=sQuery(id+"F2.wireOp",EDGE,"E11.left");var subQ11=sQuery(id+"F2.wireOp",EDGE,"E11.top");var subQ12=sQuery(id+"F2.wireOp",EDGE,"E13.top");var subQ13=sQuery(id+"F2.wireOp",EDGE,"E10.top");var subQ14=sQuery(id+"F2.wireOp",EDGE,"E12.left");var subQ15=sQuery(id+"F2.wireOp",EDGE,"E10.left");Q0=makeQuery(id+"F13.boolean.opBoolean","SPLIT",FACE,{"disambiguationData":[TD([makeQuery(id+"F1.opExtrude","SWEPT_FACE",FACE,{"disambiguationData":[OSD([sQuery(id+"F0.wireOp",EDGE,"E0.left")])]})])],"derivedFrom":makeQuery(id+"F5.boolean.opBoolean","MERGE",FACE,{"derivedFrom":[makeQuery(id+"F3.opExtrude","CAP_FACE",FACE,{"disambiguationData":[OSD([subQ13,subQ15,sQuery(id+"F2.wireOp",EDGE,"E10.right"),subQ8,subQ14,sQuery(id+"F2.wireOp",EDGE,"E12.right")])],"isStart":false}),makeQuery(id+"F3.opExtrude","CAP_FACE",FACE,{"disambiguationData":[OSD([subQ11,subQ10,sQuery(id+"F2.wireOp",EDGE,"E11.right"),subQ12,subQ9,sQuery(id+"F2.wireOp",EDGE,"E13.right")])],"isStart":false}),makeQuery(id+"F5.opExtrude","SWEPT_FACE",FACE,{"disambiguationData":[OSD([subQ7])]})]})});}
            var sketch = newSketch(context, id + "F24", { "sketchPlane" : qUnion([Q0])});
            skCircle(sketch, "E100.4", {"center": v(-18, 61.5) * mm, "radius": 1.7 * mm});
            skCircle(sketch, "E100.5", {"center": v(-103.3, 61.5) * mm, "radius": 1.7 * mm});
            skCircle(sketch, "E100.7", {"center": v(-9, 5) * mm, "radius": 2.2 * mm});
            skPoint(sketch, "E100.0.start.orphan", {"position": v(0, 0) * mm});
            skPoint(sketch, "E100.2.start.orphan", {"position": v(0, 0) * mm});
            skSolve(sketch);
        }
        {
            var Q0;
            Q0=qSketchRegion(id+"F24",true);
            extrude(context, id + "F25", {"entities" : qUnion([Q0]), "operationType" : NewBodyOperationType.REMOVE, "oppositeDirection" : true, "depth" : 25 * mm});
        }
        {
            var Q0;
            Q0=makeQuery(id+"F5.boolean.opBoolean","MERGE",FACE,{"derivedFrom":[makeQuery(id+"F3.boolean.opBoolean","MERGE",FACE,{"derivedFrom":[makeQuery(id+"F1.opExtrude","SWEPT_FACE",FACE,{"disambiguationData":[OSD([sQuery(id+"F0.wireOp",EDGE,"E0.right")])]}),makeQuery(id+"F3.opExtrude","SWEPT_FACE",FACE,{"disambiguationData":[OSD([sQuery(id+"F2.wireOp",EDGE,"E10.left"),sQuery(id+"F2.wireOp",EDGE,"E12.left")])]})]}),makeQuery(id+"F5.opExtrude","CAP_FACE",FACE,{"disambiguationData":[OSD([sQuery(id+"F4.wireOp",EDGE,"E14"),sQuery(id+"F4.wireOp",EDGE,"E15"),sQuery(id+"F4.wireOp",EDGE,"E16"),sQuery(id+"F4.wireOp",EDGE,"E17"),sQuery(id+"F4.wireOp",EDGE,"E18"),sQuery(id+"F4.wireOp",EDGE,"E19"),sQuery(id+"F4.wireOp",EDGE,"E20"),sQuery(id+"F4.wireOp",EDGE,"E21")])],"isStart":false})]});
            var sketch = newSketch(context, id + "F26", { "sketchPlane" : qUnion([Q0])});
            skCircle(sketch, "E101", {"center": v(5.3, -15.7) * mm, "radius": 4 * mm});
            skSolve(sketch);
        }
        {
            var Q0;
            Q0=qSketchRegion(id+"F26",true);
            extrude(context, id + "F27", {"entities" : qUnion([Q0]), "operationType" : NewBodyOperationType.REMOVE, "oppositeDirection" : true, "depth" : 8 * mm});
        }
    });
